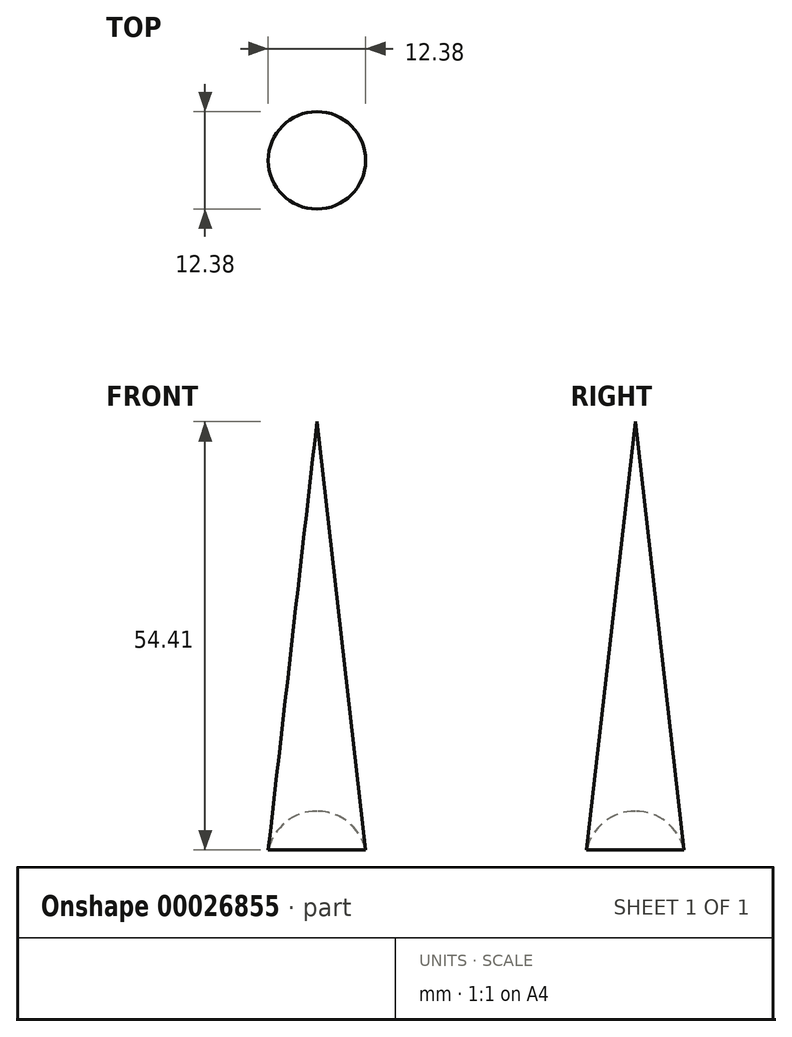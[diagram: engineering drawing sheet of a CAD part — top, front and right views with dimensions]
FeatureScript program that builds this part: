
annotation { "Feature Type Name" : "Feature", "Feature Type Description" : "" }
export const myFeature = defineFeature(function(context is Context, id is Id, definition is map)
    precondition{}
    {
        {
            var Q0;
            Q0=qCreatedBy(makeId("Front.planeOp"),FACE);
            var sketch = newSketch(context, id + "F0", { "sketchPlane" : qUnion([Q0])});
            skArc(sketch, "E0", {"start": v(-6.19, 1.43) * mm, "mid": v(-6.3, 0.72) * mm, "end": v(-6.35, 0) * mm});
            skLineSegment(sketch, "E1", {"start": v(-6.35, 0) * mm, "end": v(-6.19, 1.43) * mm});
            skLineSegment(sketch, "E2", {"start": v(6.35, 0) * mm, "end": v(0, 55.84) * mm});
            skLineSegment(sketch, "E3", {"start": v(0, 55.84) * mm, "end": v(0, 6.35) * mm});
            skArc(sketch, "E4.trimOffspring", {"start": v(6.35, 0) * mm, "mid": v(4.5, 4.5) * mm, "end": v(0, 6.35) * mm});
            skSolve(sketch);
        }
        {
            var Q0;
            {var subQ3=sQuery(id+"F0.wireOp",EDGE,"E3");Q0=makeQuery(id+"F0.imprint","IMPRINT",FACE,{"disambiguationData":[TD([[makeQuery(id+"F0.imprint","IMPRINT",EDGE,{"derivedFrom":subQ3}),1.0]])]});}
            var Q1;
            Q1=sQuery(id+"F0.wireOp",EDGE,"E3");
            revolve(context, id + "F1", {"entities" : qUnion([Q0]), "axis" : qUnion([Q1]), "revolveType" : RevolveType.FULL});
        }
    });
